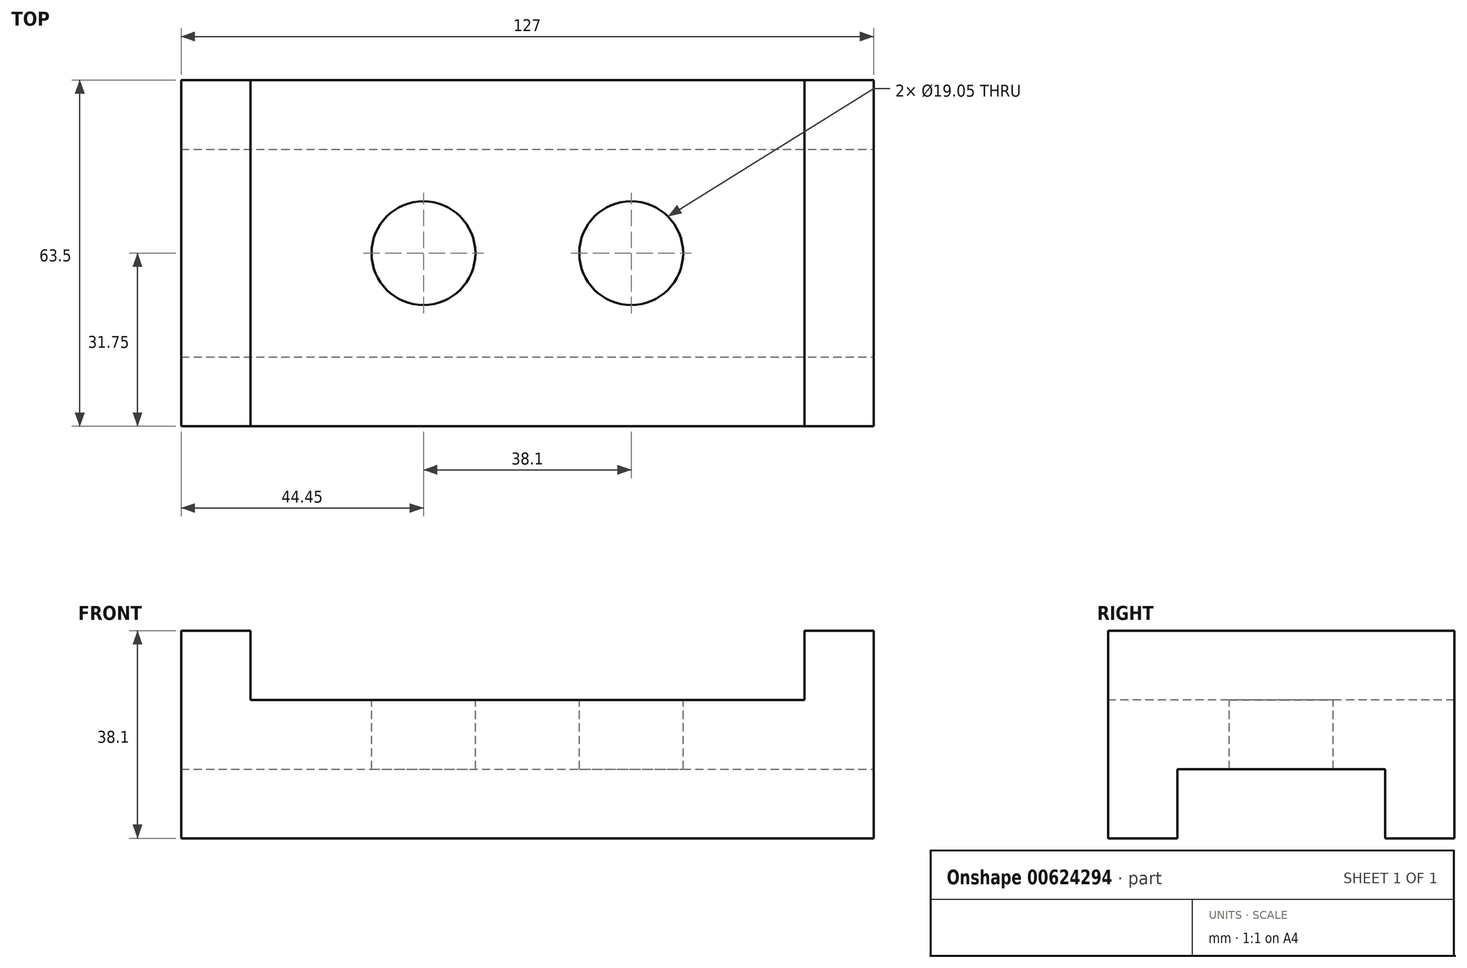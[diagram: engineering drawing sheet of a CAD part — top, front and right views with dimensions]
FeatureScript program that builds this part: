
annotation { "Feature Type Name" : "Feature", "Feature Type Description" : "" }
export const myFeature = defineFeature(function(context is Context, id is Id, definition is map)
    precondition{}
    {
        {
            var Q0;
            Q0=qCreatedBy(makeId("Top.planeOp"),FACE);
            var sketch = newSketch(context, id + "F0", { "sketchPlane" : qUnion([Q0])});
            skLineSegment(sketch, "E0.bottom", {"start": v(0, 0) * mm, "end": v(-127, 0) * mm});
            skLineSegment(sketch, "E0.top", {"start": v(0, -63.5) * mm, "end": v(-127, -63.5) * mm});
            skLineSegment(sketch, "E0.left", {"start": v(0, 0) * mm, "end": v(0, -63.5) * mm});
            skLineSegment(sketch, "E0.right", {"start": v(-127, 0) * mm, "end": v(-127, -63.5) * mm});
            skSolve(sketch);
        }
        {
            var Q0;
            Q0=makeQuery(id+"F0.imprint","IMPRINT",FACE,{"disambiguationData":[TD([[makeQuery(id+"F0.imprint","IMPRINT",EDGE,{"derivedFrom":sQuery(id+"F0.wireOp",EDGE,"E0.bottom")}),1.0]])]});
            extrude(context, id + "F1", {"entities" : qUnion([Q0]), "depth" : 38.1 * mm, "offsetDistance" : 25.4 * mm});
        }
        {
            var Q0;
            Q0=makeQuery(id+"F1.opExtrude","SWEPT_FACE",FACE,{"disambiguationData":[OSD([sQuery(id+"F0.wireOp",EDGE,"E0.top")])]});
            var sketch = newSketch(context, id + "F2", { "sketchPlane" : qUnion([Q0])});
            skLineSegment(sketch, "E1", {"start": v(0, 38.1) * mm, "end": v(-12.7, 38.1) * mm});
            skLineSegment(sketch, "E2", {"start": v(-12.7, 38.1) * mm, "end": v(-12.7, 25.4) * mm});
            skLineSegment(sketch, "E3", {"start": v(-12.7, 25.4) * mm, "end": v(-114.3, 25.4) * mm});
            skLineSegment(sketch, "E4", {"start": v(-114.3, 25.4) * mm, "end": v(-114.3, 38.1) * mm});
            skSolve(sketch);
        }
        {
            var Q0;
            {var subQ0=sQuery(id+"F2.wireOp",EDGE,"E2");Q0=makeQuery(id+"F2.imprint","IMPRINT",FACE,{"disambiguationData":[TD([[makeQuery(id+"F2.imprint","IMPRINT",EDGE,{"derivedFrom":subQ0}),-1.0]])]});}
            extrude(context, id + "F3", {"entities" : qUnion([Q0]), "operationType" : NewBodyOperationType.REMOVE, "oppositeDirection" : true, "depth" : 66.04 * mm, "offsetDistance" : 25.4 * mm});
        }
        {
            var Q0;
            Q0=makeQuery(id+"F3.boolean.opBoolean","COPY",FACE,{"derivedFrom":makeQuery(id+"F3.opExtrude","SWEPT_FACE",FACE,{"disambiguationData":[OSD([sQuery(id+"F2.wireOp",EDGE,"E3")])]})});
            var sketch = newSketch(context, id + "F4", { "sketchPlane" : qUnion([Q0])});
            skCircle(sketch, "E5", {"center": v(-82.55, -31.75) * mm, "radius": 9.53 * mm});
            skCircle(sketch, "E6", {"center": v(-44.45, -31.75) * mm, "radius": 9.53 * mm});
            skSolve(sketch);
        }
        {
            var Q0;
            Q0=makeQuery(id+"F4.imprint","IMPRINT",FACE,{"disambiguationData":[TD([[makeQuery(id+"F4.imprint","IMPRINT",EDGE,{"derivedFrom":sQuery(id+"F4.wireOp",EDGE,"E5")}),1.0]])]});
            var Q1;
            Q1=makeQuery(id+"F4.imprint","IMPRINT",FACE,{"disambiguationData":[TD([[makeQuery(id+"F4.imprint","IMPRINT",EDGE,{"derivedFrom":sQuery(id+"F4.wireOp",EDGE,"E6")}),1.0]])]});
            extrude(context, id + "F5", {"entities" : qUnion([Q0, Q1]), "operationType" : NewBodyOperationType.REMOVE, "oppositeDirection" : true, "depth" : 50.8 * mm, "offsetDistance" : 25.4 * mm});
        }
        {
            var Q0;
            Q0=makeQuery(id+"F1.opExtrude","SWEPT_FACE",FACE,{"disambiguationData":[OSD([sQuery(id+"F0.wireOp",EDGE,"E0.left")])]});
            var sketch = newSketch(context, id + "F6", { "sketchPlane" : qUnion([Q0])});
            skLineSegment(sketch, "E7", {"start": v(-50.8, 0) * mm, "end": v(-50.8, 12.7) * mm});
            skLineSegment(sketch, "E8", {"start": v(-50.8, 12.7) * mm, "end": v(-12.7, 12.7) * mm});
            skLineSegment(sketch, "E9", {"start": v(-12.7, 12.7) * mm, "end": v(-12.7, 0) * mm});
            skSolve(sketch);
        }
        {
            var Q0;
            {var subQ0=sQuery(id+"F6.wireOp",EDGE,"E7");Q0=makeQuery(id+"F6.imprint","IMPRINT",FACE,{"disambiguationData":[TD([[makeQuery(id+"F6.imprint","IMPRINT",EDGE,{"derivedFrom":subQ0}),-1.0]])]});}
            extrude(context, id + "F7", {"entities" : qUnion([Q0]), "operationType" : NewBodyOperationType.REMOVE, "oppositeDirection" : true, "depth" : 152.4 * mm, "offsetDistance" : 25.4 * mm});
        }
    });
